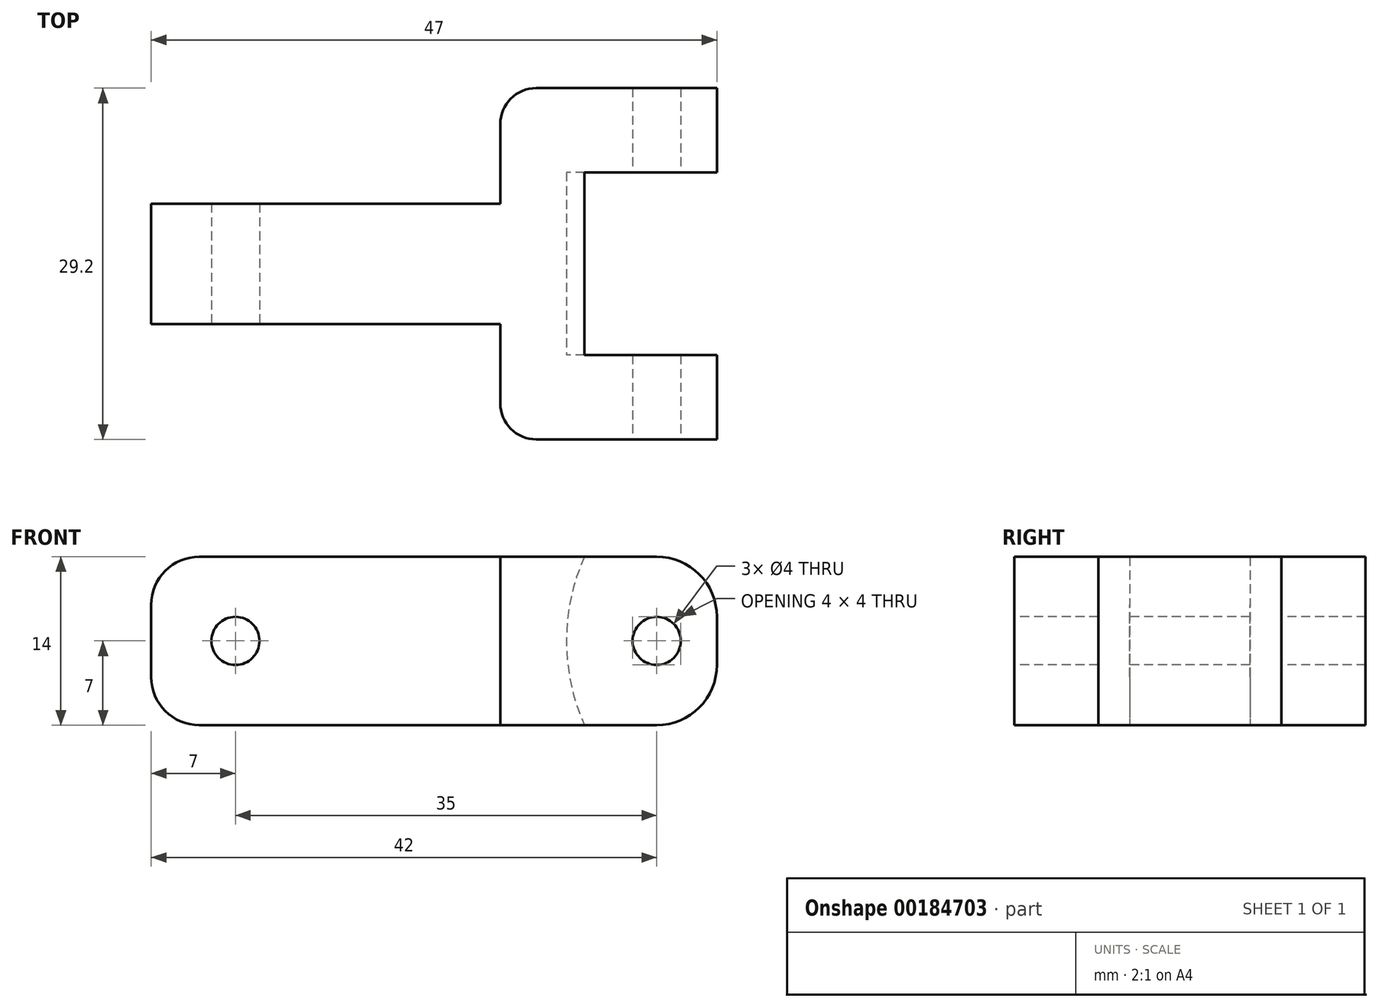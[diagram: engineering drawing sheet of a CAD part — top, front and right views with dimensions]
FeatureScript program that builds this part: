
annotation { "Feature Type Name" : "Feature", "Feature Type Description" : "" }
export const myFeature = defineFeature(function(context is Context, id is Id, definition is map)
    precondition{}
    {
        {
            var Q0;
            Q0=qCreatedBy(makeId("Front.planeOp"),FACE);
            var sketch = newSketch(context, id + "F0", { "sketchPlane" : qUnion([Q0])});
            skLineSegment(sketch, "E0.bottom", {"start": v(4, 0) * mm, "end": v(29, 0) * mm});
            skLineSegment(sketch, "E0.top", {"start": v(4, 14) * mm, "end": v(29, 14) * mm});
            skLineSegment(sketch, "E0.left", {"start": v(0, 4) * mm, "end": v(0, 10) * mm});
            skLineSegment(sketch, "E0.right", {"start": v(29, 0) * mm, "end": v(29, 14) * mm});
            skLineSegment(sketch, "E1.bottom", {"start": v(29, 0) * mm, "end": v(42, 0) * mm});
            skLineSegment(sketch, "E1.top", {"start": v(29, 14) * mm, "end": v(42, 14) * mm});
            skLineSegment(sketch, "E1.right", {"start": v(47, 5) * mm, "end": v(47, 9) * mm});
            skCircle(sketch, "E2", {"center": v(42, 7) * mm, "radius": 2 * mm});
            skPoint(sketch, "E2.centerSnap0", {"position": v(47, 7) * mm});
            skCircle(sketch, "E3", {"center": v(7, 7) * mm, "radius": 2 * mm});
            skPoint(sketch, "E4.visualSharp", {"position": v(0, 14) * mm});
            skPoint(sketch, "E5.visualSharp", {"position": v(0, 0) * mm});
            skPoint(sketch, "E6", {"position": v(49, 7) * mm});
            skArc(sketch, "E7", {"start": v(36, 14) * mm, "mid": v(34.5, 7) * mm, "end": v(36, 0) * mm});
            skPoint(sketch, "E8", {"position": v(36, 14) * mm});
            skLineSegment(sketch, "E9", {"start": v(36, 14) * mm, "end": v(36, 0) * mm});
            skPoint(sketch, "E10.visualSharp", {"position": v(47, 14) * mm});
            skArc(sketch, "E10.filletArc", {"start": v(47, 9) * mm, "mid": v(45.54, 12.54) * mm, "end": v(42, 14) * mm});
            skPoint(sketch, "E11.visualSharp", {"position": v(47, 0) * mm});
            skArc(sketch, "E11.filletArc", {"start": v(42, 0) * mm, "mid": v(45.54, 1.46) * mm, "end": v(47, 5) * mm});
            skLineSegment(sketch, "E12", {"start": v(42, 14) * mm, "end": v(47, 14) * mm});
            skLineSegment(sketch, "E13", {"start": v(47, 9) * mm, "end": v(47, 14) * mm});
            skLineSegment(sketch, "E14", {"start": v(47, 0) * mm, "end": v(42, 0) * mm});
            skLineSegment(sketch, "E15", {"start": v(47, 0) * mm, "end": v(47, 5) * mm});
            skArc(sketch, "E16.filletArc", {"start": v(4, 14) * mm, "mid": v(1.17, 12.83) * mm, "end": v(0, 10) * mm});
            skArc(sketch, "E17.filletArc", {"start": v(0, 4) * mm, "mid": v(1.17, 1.17) * mm, "end": v(4, 0) * mm});
            skSolve(sketch);
        }
        {
            var Q0;
            Q0=qCreatedBy(makeId("Top.planeOp"),FACE);
            var sketch = newSketch(context, id + "F1", { "sketchPlane" : qUnion([Q0])});
            skLineSegment(sketch, "E18.bottom", {"start": v(32, -14.6) * mm, "end": v(47, -14.6) * mm});
            skLineSegment(sketch, "E18.top", {"start": v(32, 14.6) * mm, "end": v(47, 14.6) * mm});
            skLineSegment(sketch, "E18.left", {"start": v(29, -11.6) * mm, "end": v(29, 11.6) * mm});
            skLineSegment(sketch, "E18.right", {"start": v(47, -14.6) * mm, "end": v(47, 14.6) * mm});
            skPoint(sketch, "E19", {"position": v(29, 0) * mm});
            skLineSegment(sketch, "E20.bottom", {"start": v(47, -7.6) * mm, "end": v(36, -7.6) * mm});
            skLineSegment(sketch, "E20.top", {"start": v(47, 7.6) * mm, "end": v(36, 7.6) * mm});
            skLineSegment(sketch, "E20.left", {"start": v(47, -7.6) * mm, "end": v(47, 7.6) * mm});
            skLineSegment(sketch, "E20.right", {"start": v(36, -7.6) * mm, "end": v(36, 7.6) * mm});
            skPoint(sketch, "E21", {"position": v(47, 0) * mm});
            skLineSegment(sketch, "E22", {"start": v(36, -5) * mm, "end": v(29, -5) * mm});
            skLineSegment(sketch, "E23", {"start": v(74.66, 0) * mm, "end": v(85.1, 0) * mm, "construction": true});
            skPoint(sketch, "E23.startSnap0", {"position": v(36, 0) * mm});
            skLineSegment(sketch, "E24.MirrorCS", {"start": v(36, 5) * mm, "end": v(29, 5) * mm});
            skPoint(sketch, "E25.visualSharp", {"position": v(29, 14.6) * mm});
            skArc(sketch, "E25.filletArc", {"start": v(32, 14.6) * mm, "mid": v(29.88, 13.72) * mm, "end": v(29, 11.6) * mm});
            skPoint(sketch, "E26.visualSharp", {"position": v(29, -14.6) * mm});
            skArc(sketch, "E26.filletArc", {"start": v(29, -11.6) * mm, "mid": v(29.88, -13.72) * mm, "end": v(32, -14.6) * mm});
            skSolve(sketch);
        }
        {
            var Q0;
            {var subQ1=sQuery(id+"F0.wireOp",EDGE,"E0.bottom");Q0=makeQuery(id+"F0.imprint","IMPRINT",FACE,{"disambiguationData":[TD([[makeQuery(id+"F0.imprint","IMPRINT",EDGE,{"derivedFrom":subQ1}),1.0]])]});}
            var Q1;
            {var subQ6=sQuery(id+"F0.wireOp",EDGE,"E7");Q1=makeQuery(id+"F0.imprint","IMPRINT",FACE,{"disambiguationData":[TD([[makeQuery(id+"F0.imprint","IMPRINT",EDGE,{"derivedFrom":subQ6}),-1.0]])]});}
            extrude(context, id + "F2", {"entities" : qUnion([Q0, Q1]), "oppositeDirection" : true, "depth" : 5 * mm, "hasSecondDirection" : true, "secondDirectionOppositeDirection" : false, "secondDirectionDepth" : 5 * mm});
        }
        {
            var Q0;
            {var subQ2=sQuery(id+"F1.wireOp",EDGE,"E18.top");Q0=makeQuery(id+"F1.imprint","IMPRINT",FACE,{"disambiguationData":[TD([[makeQuery(id+"F1.imprint","IMPRINT",EDGE,{"derivedFrom":subQ2}),-1.0]])]});}
            var Q1;
            {var subQ2=sQuery(id+"F1.wireOp",EDGE,"E18.bottom");Q1=makeQuery(id+"F1.imprint","IMPRINT",FACE,{"disambiguationData":[TD([[makeQuery(id+"F1.imprint","IMPRINT",EDGE,{"derivedFrom":subQ2}),1.0]])]});}
            extrude(context, id + "F3", {"entities" : qUnion([Q0, Q1]), "operationType" : NewBodyOperationType.ADD, "depth" : 14 * mm});
        }
        {
            var Q0;
            Q0=makeQuery(id+"F0.imprint","IMPRINT",FACE,{"disambiguationData":[TD([[makeQuery(id+"F0.imprint","IMPRINT",EDGE,{"derivedFrom":sQuery(id+"F0.wireOp",EDGE,"E2")}),1.0]])]});
            var Q1;
            Q1=makeQuery(id+"F0.imprint","IMPRINT",FACE,{"disambiguationData":[TD([[makeQuery(id+"F0.imprint","IMPRINT",EDGE,{"derivedFrom":sQuery(id+"F0.wireOp",EDGE,"E10.filletArc")}),-1.0]])]});
            var Q2;
            Q2=makeQuery(id+"F0.imprint","IMPRINT",FACE,{"disambiguationData":[TD([[makeQuery(id+"F0.imprint","IMPRINT",EDGE,{"derivedFrom":sQuery(id+"F0.wireOp",EDGE,"E11.filletArc")}),-1.0]])]});
            extrude(context, id + "F4", {"entities" : qUnion([Q0, Q1, Q2]), "operationType" : NewBodyOperationType.REMOVE, "oppositeDirection" : true, "depth" : 25 * mm, "hasSecondDirection" : true, "secondDirectionOppositeDirection" : false, "secondDirectionDepth" : 25 * mm});
        }
        {
            var Q0;
            Q0=makeQuery(id+"F0.imprint","IMPRINT",FACE,{"disambiguationData":[TD([[makeQuery(id+"F0.imprint","IMPRINT",EDGE,{"derivedFrom":sQuery(id+"F0.wireOp",EDGE,"E7")}),1.0]])]});
            extrude(context, id + "F5", {"entities" : qUnion([Q0]), "operationType" : NewBodyOperationType.REMOVE, "oppositeDirection" : true, "depth" : 7.6 * mm, "hasSecondDirection" : true, "secondDirectionOppositeDirection" : false, "secondDirectionDepth" : 7.6 * mm});
        }
    });
